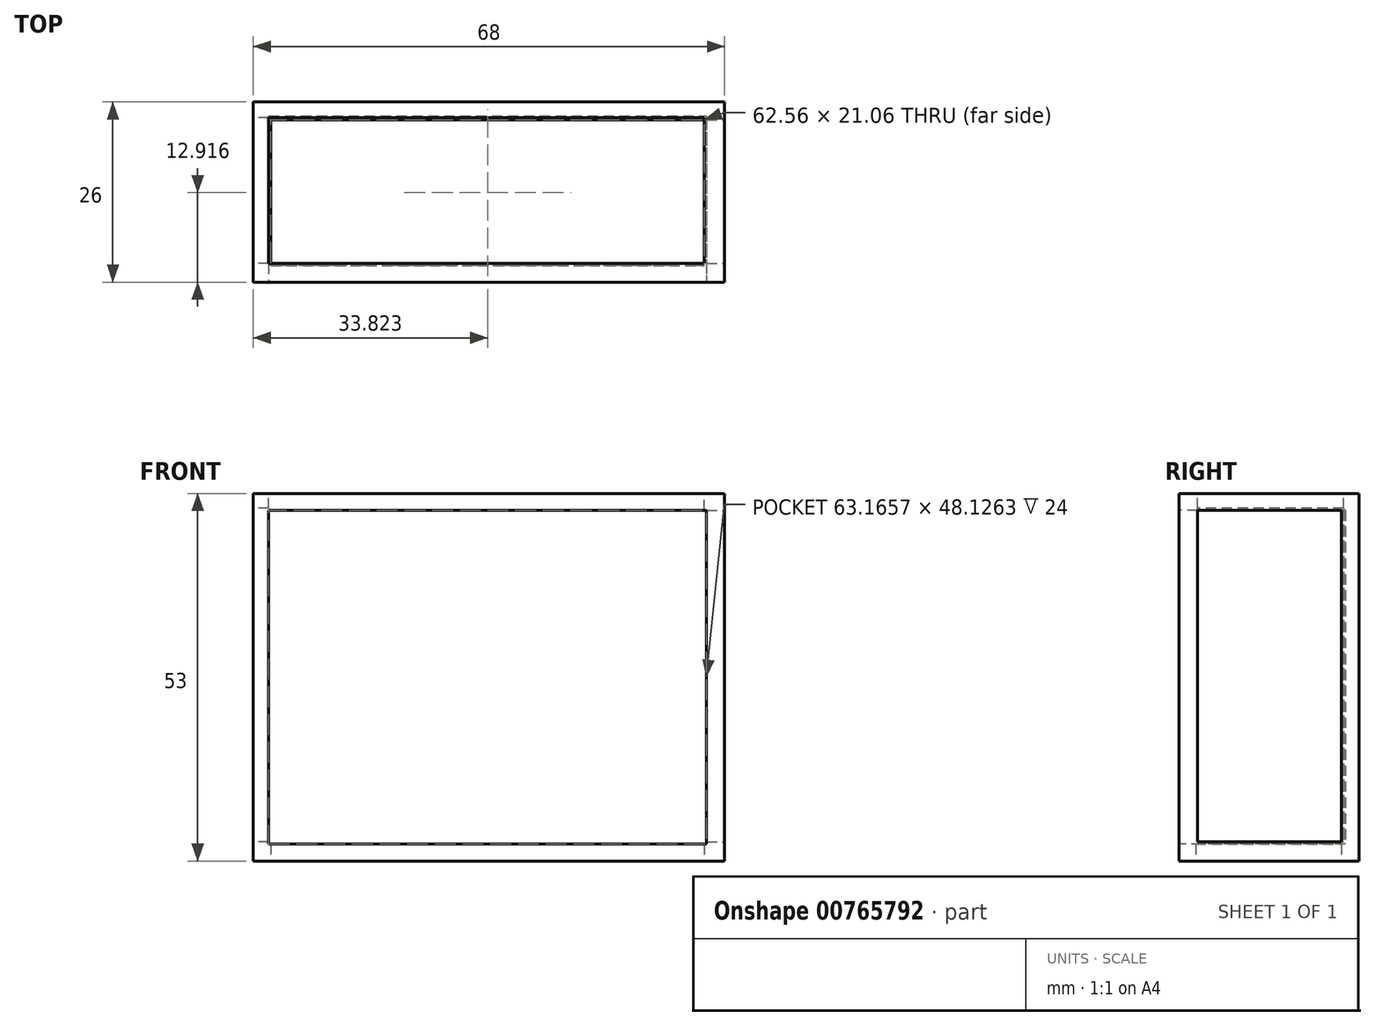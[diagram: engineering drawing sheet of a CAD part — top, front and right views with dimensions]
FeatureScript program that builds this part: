
annotation { "Feature Type Name" : "Feature", "Feature Type Description" : "" }
export const myFeature = defineFeature(function(context is Context, id is Id, definition is map)
    precondition{}
    {
        {
            var Q0;
            Q0=qCreatedBy(makeId("Front.planeOp"),FACE);
            var sketch = newSketch(context, id + "F0", { "sketchPlane" : qUnion([Q0])});
            skLineSegment(sketch, "E0.bottom", {"start": v(-43.9, 55.8) * mm, "end": v(24.1, 55.8) * mm});
            skLineSegment(sketch, "E0.top", {"start": v(-43.9, 2.8) * mm, "end": v(24.1, 2.8) * mm});
            skLineSegment(sketch, "E0.left", {"start": v(-43.9, 55.8) * mm, "end": v(-43.9, 2.8) * mm});
            skLineSegment(sketch, "E0.right", {"start": v(24.1, 55.8) * mm, "end": v(24.1, 2.8) * mm});
            skSolve(sketch);
        }
        {
            var Q0;
            Q0 = qSketchRegion(id + "F0", true);
            extrude(context, id + "F1", {"entities" : qUnion([Q0]), "depth" : 26 * mm, "offsetDistance" : 25.4 * mm});
        }
        {
            var Q0;
            Q0=makeQuery(id+"F1.opExtrude","CAP_FACE",FACE,{"disambiguationData":[OSD([sQuery(id+"F0.wireOp",EDGE,"E0.bottom"),sQuery(id+"F0.wireOp",EDGE,"E0.top"),sQuery(id+"F0.wireOp",EDGE,"E0.left"),sQuery(id+"F0.wireOp",EDGE,"E0.right")])],"isStart":false});
            var sketch = newSketch(context, id + "F2", { "sketchPlane" : qUnion([Q0])});
            skLineSegment(sketch, "E1.bottom", {"start": v(-41.66, 53.4) * mm, "end": v(21.5, 53.4) * mm});
            skLineSegment(sketch, "E1.top", {"start": v(-41.66, 5.26) * mm, "end": v(21.5, 5.26) * mm});
            skLineSegment(sketch, "E1.left", {"start": v(-41.66, 53.4) * mm, "end": v(-41.66, 5.26) * mm});
            skLineSegment(sketch, "E1.right", {"start": v(21.5, 53.4) * mm, "end": v(21.5, 5.26) * mm});
            skSolve(sketch);
        }
        {
            var Q0;
            Q0 = qSketchRegion(id + "F2", true);
            extrude(context, id + "F3", {"entities" : qUnion([Q0]), "operationType" : NewBodyOperationType.REMOVE, "oppositeDirection" : true, "depth" : 24 * mm, "offsetDistance" : 25.4 * mm});
        }
        {
            var Q0;
            Q0=makeQuery(id+"F1.opExtrude","SWEPT_FACE",FACE,{"disambiguationData":[OSD([sQuery(id+"F0.wireOp",EDGE,"E0.right")])]});
            var sketch = newSketch(context, id + "F4", { "sketchPlane" : qUnion([Q0])});
            skLineSegment(sketch, "E2.bottom", {"start": v(-23.31, 53.4) * mm, "end": v(-2.56, 53.4) * mm});
            skLineSegment(sketch, "E2.top", {"start": v(-23.31, 5.56) * mm, "end": v(-2.56, 5.56) * mm});
            skLineSegment(sketch, "E2.left", {"start": v(-23.31, 53.4) * mm, "end": v(-23.31, 5.56) * mm});
            skLineSegment(sketch, "E2.right", {"start": v(-2.56, 53.4) * mm, "end": v(-2.56, 5.56) * mm});
            skSolve(sketch);
        }
        {
            var Q0;
            Q0 = qSketchRegion(id + "F4", true);
            extrude(context, id + "F5", {"entities" : qUnion([Q0]), "operationType" : NewBodyOperationType.REMOVE, "oppositeDirection" : true, "depth" : 25.4 * mm, "offsetDistance" : 25.4 * mm});
        }
        {
            var Q0;
            Q0=makeQuery(id+"F1.opExtrude","SWEPT_FACE",FACE,{"disambiguationData":[OSD([sQuery(id+"F0.wireOp",EDGE,"E0.top")])]});
            var sketch = newSketch(context, id + "F6", { "sketchPlane" : qUnion([Q0])});
            skLineSegment(sketch, "E3.bottom", {"start": v(-41.36, 23.61) * mm, "end": v(21.2, 23.61) * mm});
            skLineSegment(sketch, "E3.top", {"start": v(-41.36, 2.56) * mm, "end": v(21.2, 2.56) * mm});
            skLineSegment(sketch, "E3.left", {"start": v(-41.36, 23.61) * mm, "end": v(-41.36, 2.56) * mm});
            skLineSegment(sketch, "E3.right", {"start": v(21.2, 23.61) * mm, "end": v(21.2, 2.56) * mm});
            skSolve(sketch);
        }
        {
            var Q0;
            Q0 = qSketchRegion(id + "F6", true);
            extrude(context, id + "F7", {"entities" : qUnion([Q0]), "operationType" : NewBodyOperationType.REMOVE, "oppositeDirection" : true, "depth" : 25.4 * mm, "offsetDistance" : 25.4 * mm});
        }
        {
            var Q0;
            Q0=makeQuery(id+"F1.opExtrude","SWEPT_FACE",FACE,{"disambiguationData":[OSD([sQuery(id+"F0.wireOp",EDGE,"E0.bottom")])]});
            var sketch = newSketch(context, id + "F8", { "sketchPlane" : qUnion([Q0])});
            skLineSegment(sketch, "E4.bottom", {"start": v(-41.66, -2.26) * mm, "end": v(21.2, -2.26) * mm});
            skLineSegment(sketch, "E4.top", {"start": v(-41.66, -23.31) * mm, "end": v(21.2, -23.31) * mm});
            skLineSegment(sketch, "E4.left", {"start": v(-41.66, -2.26) * mm, "end": v(-41.66, -23.31) * mm});
            skLineSegment(sketch, "E4.right", {"start": v(21.2, -2.26) * mm, "end": v(21.2, -23.31) * mm});
            skSolve(sketch);
        }
        {
            var Q0;
            Q0 = qSketchRegion(id + "F8", true);
            extrude(context, id + "F9", {"entities" : qUnion([Q0]), "operationType" : NewBodyOperationType.REMOVE, "oppositeDirection" : true, "depth" : 25.4 * mm, "offsetDistance" : 25.4 * mm});
        }
        {
            var Q0;
            Q0=makeQuery(id+"F1.opExtrude","SWEPT_FACE",FACE,{"disambiguationData":[OSD([sQuery(id+"F0.wireOp",EDGE,"E0.left")])]});
            var sketch = newSketch(context, id + "F10", { "sketchPlane" : qUnion([Q0])});
            skLineSegment(sketch, "E5.bottom", {"start": v(2.26, 53.7) * mm, "end": v(23.31, 53.7) * mm});
            skLineSegment(sketch, "E5.top", {"start": v(2.26, 5.56) * mm, "end": v(23.31, 5.56) * mm});
            skLineSegment(sketch, "E5.left", {"start": v(2.26, 53.7) * mm, "end": v(2.26, 5.56) * mm});
            skLineSegment(sketch, "E5.right", {"start": v(23.31, 53.7) * mm, "end": v(23.31, 5.56) * mm});
            skSolve(sketch);
        }
        {
            var Q0;
            Q0 = qSketchRegion(id + "F10", true);
            extrude(context, id + "F11", {"entities" : qUnion([Q0]), "operationType" : NewBodyOperationType.REMOVE, "oppositeDirection" : true, "depth" : 25.4 * mm, "offsetDistance" : 25.4 * mm});
        }
    });
